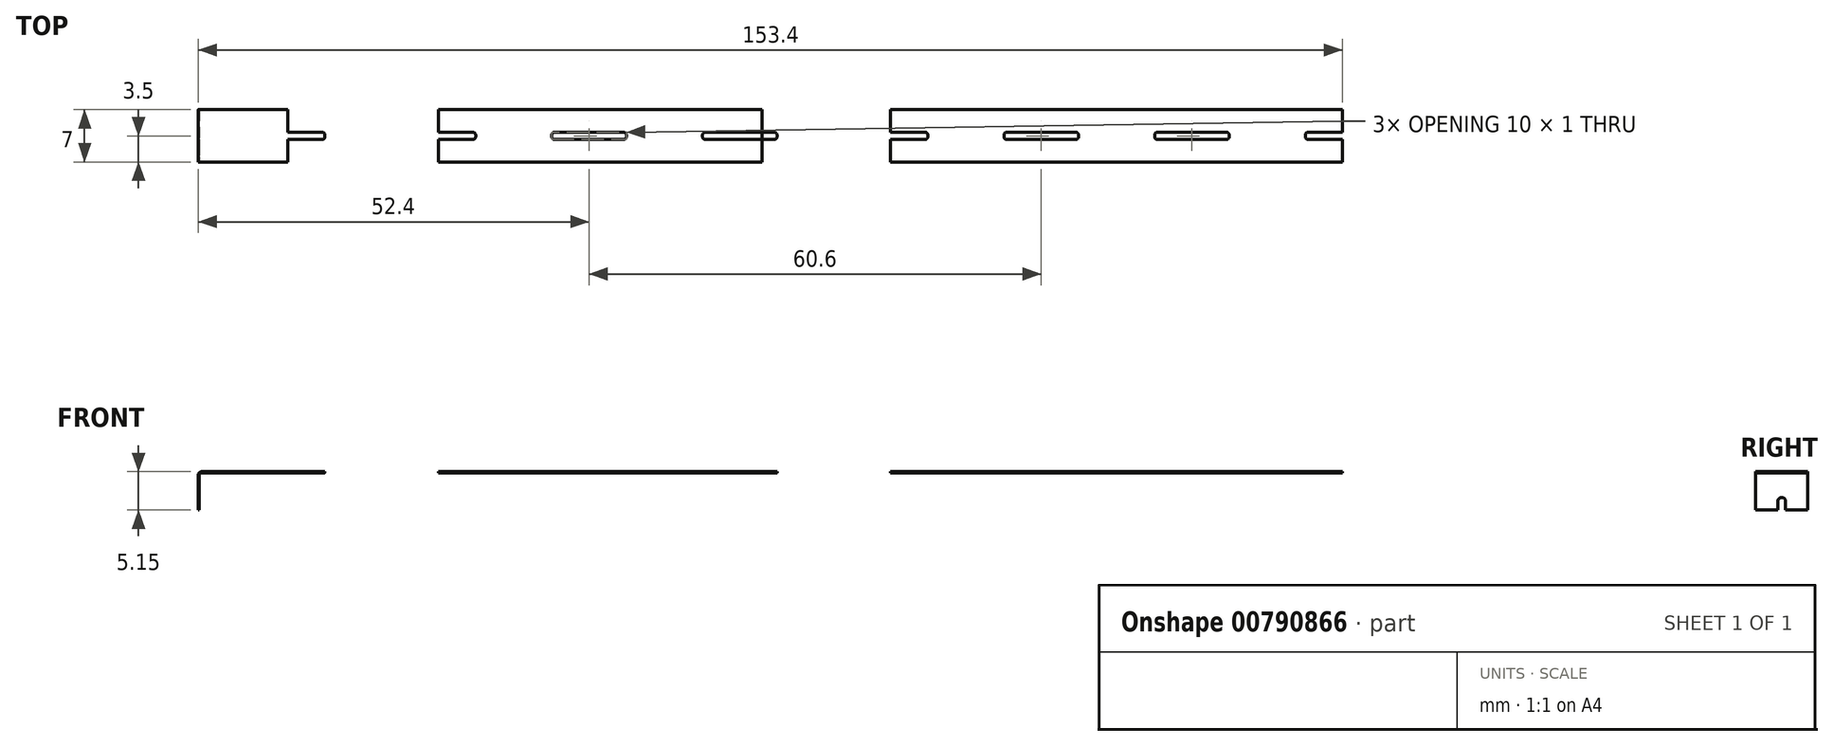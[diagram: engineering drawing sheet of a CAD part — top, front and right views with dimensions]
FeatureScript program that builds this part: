
annotation { "Feature Type Name" : "Feature", "Feature Type Description" : "" }
export const myFeature = defineFeature(function(context is Context, id is Id, definition is map)
    precondition{}
    {
        {
            var Q0;
            Q0=qCreatedBy(makeId("Top.planeOp"),FACE);
            var sketch = newSketch(context, id + "F0", { "sketchPlane" : qUnion([Q0])});
            skPoint(sketch, "E0.middle", {"position": v(0, 0) * mm});
            skLineSegment(sketch, "E1.bottom", {"start": v(-5.5, -0.5) * mm, "end": v(-10.1, -0.5) * mm});
            skLineSegment(sketch, "E1.top", {"start": v(-5.5, 0.5) * mm, "end": v(-10.1, 0.5) * mm});
            skLineSegment(sketch, "E1.left", {"start": v(-5.1, -0.1) * mm, "end": v(-5.1, 0.1) * mm});
            skLineSegment(sketch, "E1.right", {"start": v(-15.1, -0.1) * mm, "end": v(-15.1, 0.1) * mm});
            skPoint(sketch, "E1.middle", {"position": v(-10.1, 0) * mm});
            skPoint(sketch, "E2.visualSharp", {"position": v(-5.1, 0.5) * mm});
            skArc(sketch, "E2.filletArc", {"start": v(-5.1, 0.1) * mm, "mid": v(-5.22, 0.38) * mm, "end": v(-5.5, 0.5) * mm});
            skPoint(sketch, "E3.visualSharp", {"position": v(-5.1, -0.5) * mm});
            skArc(sketch, "E3.filletArc", {"start": v(-5.5, -0.5) * mm, "mid": v(-5.22, -0.38) * mm, "end": v(-5.1, -0.1) * mm});
            skPoint(sketch, "E4.visualSharp", {"position": v(-15.1, 0.5) * mm});
            skArc(sketch, "E4.filletArc", {"start": v(-14.7, 0.5) * mm, "mid": v(-14.98, 0.38) * mm, "end": v(-15.1, 0.1) * mm});
            skPoint(sketch, "E5.visualSharp", {"position": v(-15.1, -0.5) * mm});
            skArc(sketch, "E5.filletArc", {"start": v(-15.1, -0.1) * mm, "mid": v(-14.98, -0.38) * mm, "end": v(-14.7, -0.5) * mm});
            skLineSegment(sketch, "E6", {"start": v(0, 3.5) * mm, "end": v(-10.1, 3.5) * mm});
            skPoint(sketch, "E6.endSnap0", {"position": v(-10.1, 0.5) * mm});
            skLineSegment(sketch, "E7", {"start": v(-10.1, 3.5) * mm, "end": v(-10.1, 0.5) * mm});
            skLineSegment(sketch, "E8.MirrorCS", {"start": v(0, -3.5) * mm, "end": v(-10.1, -3.5) * mm});
            skLineSegment(sketch, "E9.MirrorCS", {"start": v(-10.1, -3.5) * mm, "end": v(-10.1, -0.5) * mm});
            skLineSegment(sketch, "E10.MirrorCS", {"start": v(0, 3.5) * mm, "end": v(10.1, 3.5) * mm});
            skLineSegment(sketch, "E11.MirrorCS", {"start": v(0, -3.5) * mm, "end": v(10.1, -3.5) * mm});
            skLineSegment(sketch, "E12.MirrorCS", {"start": v(5.1, -0.1) * mm, "end": v(5.1, 0.1) * mm});
            skArc(sketch, "E13.MirrorCS", {"start": v(5.1, 0.1) * mm, "mid": v(5.22, 0.38) * mm, "end": v(5.5, 0.5) * mm});
            skArc(sketch, "E14.MirrorCS", {"start": v(15.1, -0.1) * mm, "mid": v(14.98, -0.38) * mm, "end": v(14.7, -0.5) * mm});
            skLineSegment(sketch, "E15.MirrorCS", {"start": v(15.1, -0.1) * mm, "end": v(15.1, 0.1) * mm});
            skArc(sketch, "E16.MirrorCS", {"start": v(14.7, 0.5) * mm, "mid": v(14.98, 0.38) * mm, "end": v(15.1, 0.1) * mm});
            skArc(sketch, "E17.MirrorCS", {"start": v(5.5, -0.5) * mm, "mid": v(5.22, -0.38) * mm, "end": v(5.1, -0.1) * mm});
            skPoint(sketch, "E18.MirrorP", {"position": v(15.1, 0.5) * mm});
            skLineSegment(sketch, "E19.MirrorCS", {"start": v(5.5, 0.5) * mm, "end": v(14.7, 0.5) * mm});
            skLineSegment(sketch, "E20.MirrorCS", {"start": v(5.5, -0.5) * mm, "end": v(14.7, -0.5) * mm});
            skPoint(sketch, "E21.MirrorP", {"position": v(10.1, 0.5) * mm});
            skPoint(sketch, "E22.MirrorP", {"position": v(5.1, 0.5) * mm});
            skPoint(sketch, "E23.MirrorP", {"position": v(15.1, -0.5) * mm});
            skPoint(sketch, "E24.MirrorP", {"position": v(5.1, -0.5) * mm});
            skPoint(sketch, "E25.MirrorP", {"position": v(10.1, 0) * mm});
            skLineSegment(sketch, "E26.MirrorCS", {"start": v(10.1, 3.5) * mm, "end": v(10.1, 0.5) * mm});
            skLineSegment(sketch, "E27.MirrorCS", {"start": v(10.1, -3.5) * mm, "end": v(10.1, -0.5) * mm});
            skPoint(sketch, "E28.1.0.0", {"position": v(25.3, 0.5) * mm});
            skLineSegment(sketch, "E28.1.0.1", {"start": v(20.2, 3.5) * mm, "end": v(30.3, 3.5) * mm});
            skLineSegment(sketch, "E28.1.0.2", {"start": v(25.7, -0.5) * mm, "end": v(34.9, -0.5) * mm});
            skPoint(sketch, "E28.1.0.3", {"position": v(20.2, 0) * mm});
            skLineSegment(sketch, "E28.1.0.4", {"start": v(20.2, -3.5) * mm, "end": v(30.3, -3.5) * mm});
            skPoint(sketch, "E28.1.0.5", {"position": v(30.3, 0.5) * mm});
            skPoint(sketch, "E28.1.0.6", {"position": v(30.3, 0) * mm});
            skPoint(sketch, "E28.1.0.7", {"position": v(35.3, -0.5) * mm});
            skPoint(sketch, "E28.1.0.8", {"position": v(25.3, -0.5) * mm});
            skLineSegment(sketch, "E28.1.0.9", {"start": v(20.2, -3.5) * mm, "end": v(10.1, -3.5) * mm});
            skLineSegment(sketch, "E28.1.0.10", {"start": v(25.7, 0.5) * mm, "end": v(34.9, 0.5) * mm});
            skLineSegment(sketch, "E28.1.0.11", {"start": v(20.2, 3.5) * mm, "end": v(10.1, 3.5) * mm});
            skLineSegment(sketch, "E28.1.0.12", {"start": v(30.3, 3.5) * mm, "end": v(30.3, 0.5) * mm});
            skLineSegment(sketch, "E28.1.0.13", {"start": v(30.3, -3.5) * mm, "end": v(30.3, -0.5) * mm});
            skPoint(sketch, "E28.1.0.14", {"position": v(35.3, 0.5) * mm});
            skArc(sketch, "E28.1.0.15", {"start": v(34.9, 0.5) * mm, "mid": v(35.18, 0.38) * mm, "end": v(35.3, 0.1) * mm});
            skArc(sketch, "E28.1.0.16", {"start": v(25.7, -0.5) * mm, "mid": v(25.42, -0.38) * mm, "end": v(25.3, -0.1) * mm});
            skArc(sketch, "E28.1.0.17", {"start": v(35.3, -0.1) * mm, "mid": v(35.18, -0.38) * mm, "end": v(34.9, -0.5) * mm});
            skArc(sketch, "E28.1.0.18", {"start": v(25.3, 0.1) * mm, "mid": v(25.42, 0.38) * mm, "end": v(25.7, 0.5) * mm});
            skLineSegment(sketch, "E28.1.0.19", {"start": v(25.3, -0.1) * mm, "end": v(25.3, 0.1) * mm});
            skLineSegment(sketch, "E28.1.0.20", {"start": v(35.3, -0.1) * mm, "end": v(35.3, 0.1) * mm});
            skPoint(sketch, "E28.2.0.0", {"position": v(45.5, 0.5) * mm});
            skLineSegment(sketch, "E28.2.0.1", {"start": v(40.4, 3.5) * mm, "end": v(50.5, 3.5) * mm});
            skLineSegment(sketch, "E28.2.0.2", {"start": v(45.9, -0.5) * mm, "end": v(55.1, -0.5) * mm});
            skPoint(sketch, "E28.2.0.3", {"position": v(40.4, 0) * mm});
            skLineSegment(sketch, "E28.2.0.4", {"start": v(40.4, -3.5) * mm, "end": v(50.5, -3.5) * mm});
            skPoint(sketch, "E28.2.0.5", {"position": v(50.5, 0.5) * mm});
            skPoint(sketch, "E28.2.0.6", {"position": v(50.5, 0) * mm});
            skPoint(sketch, "E28.2.0.7", {"position": v(55.5, -0.5) * mm});
            skPoint(sketch, "E28.2.0.8", {"position": v(45.5, -0.5) * mm});
            skLineSegment(sketch, "E28.2.0.9", {"start": v(40.4, -3.5) * mm, "end": v(30.3, -3.5) * mm});
            skLineSegment(sketch, "E28.2.0.10", {"start": v(45.9, 0.5) * mm, "end": v(55.1, 0.5) * mm});
            skLineSegment(sketch, "E28.2.0.11", {"start": v(40.4, 3.5) * mm, "end": v(30.3, 3.5) * mm});
            skLineSegment(sketch, "E28.2.0.12", {"start": v(50.5, 3.5) * mm, "end": v(50.5, 0.5) * mm});
            skLineSegment(sketch, "E28.2.0.13", {"start": v(50.5, -3.5) * mm, "end": v(50.5, -0.5) * mm});
            skPoint(sketch, "E28.2.0.14", {"position": v(55.5, 0.5) * mm});
            skArc(sketch, "E28.2.0.15", {"start": v(55.1, 0.5) * mm, "mid": v(55.38, 0.38) * mm, "end": v(55.5, 0.1) * mm});
            skArc(sketch, "E28.2.0.16", {"start": v(45.9, -0.5) * mm, "mid": v(45.62, -0.38) * mm, "end": v(45.5, -0.1) * mm});
            skArc(sketch, "E28.2.0.17", {"start": v(55.5, -0.1) * mm, "mid": v(55.38, -0.38) * mm, "end": v(55.1, -0.5) * mm});
            skArc(sketch, "E28.2.0.18", {"start": v(45.5, 0.1) * mm, "mid": v(45.62, 0.38) * mm, "end": v(45.9, 0.5) * mm});
            skLineSegment(sketch, "E28.2.0.19", {"start": v(45.5, -0.1) * mm, "end": v(45.5, 0.1) * mm});
            skLineSegment(sketch, "E28.2.0.20", {"start": v(55.5, -0.1) * mm, "end": v(55.5, 0.1) * mm});
            skPoint(sketch, "E28.3.0.0", {"position": v(65.7, 0.5) * mm});
            skLineSegment(sketch, "E28.3.0.1", {"start": v(60.6, 3.5) * mm, "end": v(70.7, 3.5) * mm});
            skLineSegment(sketch, "E28.3.0.2", {"start": v(66.1, -0.5) * mm, "end": v(75.3, -0.5) * mm});
            skPoint(sketch, "E28.3.0.3", {"position": v(60.6, 0) * mm});
            skLineSegment(sketch, "E28.3.0.4", {"start": v(60.6, -3.5) * mm, "end": v(70.7, -3.5) * mm});
            skPoint(sketch, "E28.3.0.5", {"position": v(70.7, 0.5) * mm});
            skPoint(sketch, "E28.3.0.6", {"position": v(70.7, 0) * mm});
            skPoint(sketch, "E28.3.0.7", {"position": v(75.7, -0.5) * mm});
            skPoint(sketch, "E28.3.0.8", {"position": v(65.7, -0.5) * mm});
            skLineSegment(sketch, "E28.3.0.9", {"start": v(60.6, -3.5) * mm, "end": v(50.5, -3.5) * mm});
            skLineSegment(sketch, "E28.3.0.10", {"start": v(66.1, 0.5) * mm, "end": v(75.3, 0.5) * mm});
            skLineSegment(sketch, "E28.3.0.11", {"start": v(60.6, 3.5) * mm, "end": v(50.5, 3.5) * mm});
            skLineSegment(sketch, "E28.3.0.12", {"start": v(70.7, 3.5) * mm, "end": v(70.7, 0.5) * mm});
            skLineSegment(sketch, "E28.3.0.13", {"start": v(70.7, -3.5) * mm, "end": v(70.7, -0.5) * mm});
            skPoint(sketch, "E28.3.0.14", {"position": v(75.7, 0.5) * mm});
            skArc(sketch, "E28.3.0.15", {"start": v(75.3, 0.5) * mm, "mid": v(75.58, 0.38) * mm, "end": v(75.7, 0.1) * mm});
            skArc(sketch, "E28.3.0.16", {"start": v(66.1, -0.5) * mm, "mid": v(65.82, -0.38) * mm, "end": v(65.7, -0.1) * mm});
            skArc(sketch, "E28.3.0.17", {"start": v(75.7, -0.1) * mm, "mid": v(75.58, -0.38) * mm, "end": v(75.3, -0.5) * mm});
            skArc(sketch, "E28.3.0.18", {"start": v(65.7, 0.1) * mm, "mid": v(65.82, 0.38) * mm, "end": v(66.1, 0.5) * mm});
            skLineSegment(sketch, "E28.3.0.19", {"start": v(65.7, -0.1) * mm, "end": v(65.7, 0.1) * mm});
            skLineSegment(sketch, "E28.3.0.20", {"start": v(75.7, -0.1) * mm, "end": v(75.7, 0.1) * mm});
            skLineSegment(sketch, "E28.direction1", {"start": v(-10.1, -3.5) * mm, "end": v(10.1, -3.5) * mm, "construction": true});
            skLineSegment(sketch, "E29", {"start": v(0, 3.5) * mm, "end": v(0, -3.5) * mm});
            skLineSegment(sketch, "E30.bottom", {"start": v(70.7, -3.5) * mm, "end": v(73.7, -3.5) * mm});
            skLineSegment(sketch, "E30.top", {"start": v(70.7, 3.5) * mm, "end": v(73.7, 3.5) * mm});
            skLineSegment(sketch, "E30.left", {"start": v(70.7, -3.5) * mm, "end": v(70.7, 3.5) * mm});
            skLineSegment(sketch, "E30.right", {"start": v(73.7, -3.5) * mm, "end": v(73.7, 3.5) * mm});
            skPoint(sketch, "E31.0.4.0", {"position": v(85.9, 0.5) * mm});
            skLineSegment(sketch, "E31.1.4.0", {"start": v(80.8, 3.5) * mm, "end": v(90.9, 3.5) * mm});
            skLineSegment(sketch, "E31.4.4.0", {"start": v(86.3, -0.5) * mm, "end": v(95.5, -0.5) * mm});
            skPoint(sketch, "E31.7.4.0", {"position": v(80.8, 0) * mm});
            skLineSegment(sketch, "E31.8.4.0", {"start": v(80.8, -3.5) * mm, "end": v(90.9, -3.5) * mm});
            skPoint(sketch, "E31.11.4.0", {"position": v(90.9, 0.5) * mm});
            skPoint(sketch, "E31.12.4.0", {"position": v(90.9, 0) * mm});
            skPoint(sketch, "E31.13.4.0", {"position": v(95.9, -0.5) * mm});
            skPoint(sketch, "E31.14.4.0", {"position": v(85.9, -0.5) * mm});
            skLineSegment(sketch, "E31.15.4.0", {"start": v(80.8, -3.5) * mm, "end": v(70.7, -3.5) * mm});
            skLineSegment(sketch, "E31.18.4.0", {"start": v(86.3, 0.5) * mm, "end": v(95.5, 0.5) * mm});
            skLineSegment(sketch, "E31.21.4.0", {"start": v(80.8, 3.5) * mm, "end": v(70.7, 3.5) * mm});
            skLineSegment(sketch, "E31.24.4.0", {"start": v(90.9, 3.5) * mm, "end": v(90.9, 0.5) * mm});
            skLineSegment(sketch, "E31.27.4.0", {"start": v(90.9, -3.5) * mm, "end": v(90.9, -0.5) * mm});
            skPoint(sketch, "E31.30.4.0", {"position": v(95.9, 0.5) * mm});
            skArc(sketch, "E31.31.4.0", {"start": v(95.5, 0.5) * mm, "mid": v(95.78, 0.38) * mm, "end": v(95.9, 0.1) * mm});
            skArc(sketch, "E31.35.4.0", {"start": v(86.3, -0.5) * mm, "mid": v(86.02, -0.38) * mm, "end": v(85.9, -0.1) * mm});
            skArc(sketch, "E31.39.4.0", {"start": v(95.9, -0.1) * mm, "mid": v(95.78, -0.38) * mm, "end": v(95.5, -0.5) * mm});
            skArc(sketch, "E31.43.4.0", {"start": v(85.9, 0.1) * mm, "mid": v(86.02, 0.38) * mm, "end": v(86.3, 0.5) * mm});
            skLineSegment(sketch, "E31.47.4.0", {"start": v(85.9, -0.1) * mm, "end": v(85.9, 0.1) * mm});
            skLineSegment(sketch, "E31.50.4.0", {"start": v(95.9, -0.1) * mm, "end": v(95.9, 0.1) * mm});
            skPoint(sketch, "E31.0.5.0", {"position": v(106.1, 0.5) * mm});
            skLineSegment(sketch, "E31.1.5.0", {"start": v(101, 3.5) * mm, "end": v(111.1, 3.5) * mm});
            skLineSegment(sketch, "E31.4.5.0", {"start": v(106.5, -0.5) * mm, "end": v(115.7, -0.5) * mm});
            skPoint(sketch, "E31.7.5.0", {"position": v(101, 0) * mm});
            skLineSegment(sketch, "E31.8.5.0", {"start": v(101, -3.5) * mm, "end": v(111.1, -3.5) * mm});
            skPoint(sketch, "E31.11.5.0", {"position": v(111.1, 0.5) * mm});
            skPoint(sketch, "E31.12.5.0", {"position": v(111.1, 0) * mm});
            skPoint(sketch, "E31.13.5.0", {"position": v(116.1, -0.5) * mm});
            skPoint(sketch, "E31.14.5.0", {"position": v(106.1, -0.5) * mm});
            skLineSegment(sketch, "E31.15.5.0", {"start": v(101, -3.5) * mm, "end": v(90.9, -3.5) * mm});
            skLineSegment(sketch, "E31.18.5.0", {"start": v(106.5, 0.5) * mm, "end": v(115.7, 0.5) * mm});
            skLineSegment(sketch, "E31.21.5.0", {"start": v(101, 3.5) * mm, "end": v(90.9, 3.5) * mm});
            skLineSegment(sketch, "E31.24.5.0", {"start": v(111.1, 3.5) * mm, "end": v(111.1, 0.5) * mm});
            skLineSegment(sketch, "E31.27.5.0", {"start": v(111.1, -3.5) * mm, "end": v(111.1, -0.5) * mm});
            skPoint(sketch, "E31.30.5.0", {"position": v(116.1, 0.5) * mm});
            skArc(sketch, "E31.31.5.0", {"start": v(115.7, 0.5) * mm, "mid": v(115.98, 0.38) * mm, "end": v(116.1, 0.1) * mm});
            skArc(sketch, "E31.35.5.0", {"start": v(106.5, -0.5) * mm, "mid": v(106.22, -0.38) * mm, "end": v(106.1, -0.1) * mm});
            skArc(sketch, "E31.39.5.0", {"start": v(116.1, -0.1) * mm, "mid": v(115.98, -0.38) * mm, "end": v(115.7, -0.5) * mm});
            skArc(sketch, "E31.43.5.0", {"start": v(106.1, 0.1) * mm, "mid": v(106.22, 0.38) * mm, "end": v(106.5, 0.5) * mm});
            skLineSegment(sketch, "E31.47.5.0", {"start": v(106.1, -0.1) * mm, "end": v(106.1, 0.1) * mm});
            skLineSegment(sketch, "E31.50.5.0", {"start": v(116.1, -0.1) * mm, "end": v(116.1, 0.1) * mm});
            skPoint(sketch, "E31.0.6.0", {"position": v(126.3, 0.5) * mm});
            skLineSegment(sketch, "E31.1.6.0", {"start": v(121.2, 3.5) * mm, "end": v(131.3, 3.5) * mm});
            skLineSegment(sketch, "E31.4.6.0", {"start": v(126.7, -0.5) * mm, "end": v(135.9, -0.5) * mm});
            skPoint(sketch, "E31.7.6.0", {"position": v(121.2, 0) * mm});
            skLineSegment(sketch, "E31.8.6.0", {"start": v(121.2, -3.5) * mm, "end": v(131.3, -3.5) * mm});
            skPoint(sketch, "E31.11.6.0", {"position": v(131.3, 0.5) * mm});
            skPoint(sketch, "E31.12.6.0", {"position": v(131.3, 0) * mm});
            skPoint(sketch, "E31.13.6.0", {"position": v(136.3, -0.5) * mm});
            skPoint(sketch, "E31.14.6.0", {"position": v(126.3, -0.5) * mm});
            skLineSegment(sketch, "E31.15.6.0", {"start": v(121.2, -3.5) * mm, "end": v(111.1, -3.5) * mm});
            skLineSegment(sketch, "E31.18.6.0", {"start": v(126.7, 0.5) * mm, "end": v(135.9, 0.5) * mm});
            skLineSegment(sketch, "E31.21.6.0", {"start": v(121.2, 3.5) * mm, "end": v(111.1, 3.5) * mm});
            skLineSegment(sketch, "E31.24.6.0", {"start": v(131.3, 3.5) * mm, "end": v(131.3, 0.5) * mm});
            skLineSegment(sketch, "E31.27.6.0", {"start": v(131.3, -3.5) * mm, "end": v(131.3, -0.5) * mm});
            skPoint(sketch, "E31.30.6.0", {"position": v(136.3, 0.5) * mm});
            skArc(sketch, "E31.31.6.0", {"start": v(135.9, 0.5) * mm, "mid": v(136.18, 0.38) * mm, "end": v(136.3, 0.1) * mm});
            skArc(sketch, "E31.35.6.0", {"start": v(126.7, -0.5) * mm, "mid": v(126.42, -0.38) * mm, "end": v(126.3, -0.1) * mm});
            skArc(sketch, "E31.39.6.0", {"start": v(136.3, -0.1) * mm, "mid": v(136.18, -0.38) * mm, "end": v(135.9, -0.5) * mm});
            skArc(sketch, "E31.43.6.0", {"start": v(126.3, 0.1) * mm, "mid": v(126.42, 0.38) * mm, "end": v(126.7, 0.5) * mm});
            skLineSegment(sketch, "E31.47.6.0", {"start": v(126.3, -0.1) * mm, "end": v(126.3, 0.1) * mm});
            skLineSegment(sketch, "E31.50.6.0", {"start": v(136.3, -0.1) * mm, "end": v(136.3, 0.1) * mm});
            skPoint(sketch, "E31.0.7.0", {"position": v(146.5, 0.5) * mm});
            skLineSegment(sketch, "E31.1.7.0", {"start": v(141.4, 3.5) * mm, "end": v(151.5, 3.5) * mm});
            skLineSegment(sketch, "E31.4.7.0", {"start": v(146.9, -0.5) * mm, "end": v(156.1, -0.5) * mm});
            skPoint(sketch, "E31.7.7.0", {"position": v(141.4, 0) * mm});
            skLineSegment(sketch, "E31.8.7.0", {"start": v(141.4, -3.5) * mm, "end": v(151.5, -3.5) * mm});
            skPoint(sketch, "E31.11.7.0", {"position": v(151.5, 0.5) * mm});
            skPoint(sketch, "E31.12.7.0", {"position": v(151.5, 0) * mm});
            skPoint(sketch, "E31.13.7.0", {"position": v(156.5, -0.5) * mm});
            skPoint(sketch, "E31.14.7.0", {"position": v(146.5, -0.5) * mm});
            skLineSegment(sketch, "E31.15.7.0", {"start": v(141.4, -3.5) * mm, "end": v(131.3, -3.5) * mm});
            skLineSegment(sketch, "E31.18.7.0", {"start": v(146.9, 0.5) * mm, "end": v(156.1, 0.5) * mm});
            skLineSegment(sketch, "E31.21.7.0", {"start": v(141.4, 3.5) * mm, "end": v(131.3, 3.5) * mm});
            skLineSegment(sketch, "E31.24.7.0", {"start": v(151.5, 3.5) * mm, "end": v(151.5, 0.5) * mm});
            skLineSegment(sketch, "E31.27.7.0", {"start": v(151.5, -3.5) * mm, "end": v(151.5, -0.5) * mm});
            skPoint(sketch, "E31.30.7.0", {"position": v(156.5, 0.5) * mm});
            skArc(sketch, "E31.31.7.0", {"start": v(156.1, 0.5) * mm, "mid": v(156.38, 0.38) * mm, "end": v(156.5, 0.1) * mm});
            skArc(sketch, "E31.35.7.0", {"start": v(146.9, -0.5) * mm, "mid": v(146.62, -0.38) * mm, "end": v(146.5, -0.1) * mm});
            skArc(sketch, "E31.39.7.0", {"start": v(156.5, -0.1) * mm, "mid": v(156.38, -0.38) * mm, "end": v(156.1, -0.5) * mm});
            skArc(sketch, "E31.43.7.0", {"start": v(146.5, 0.1) * mm, "mid": v(146.62, 0.38) * mm, "end": v(146.9, 0.5) * mm});
            skLineSegment(sketch, "E31.47.7.0", {"start": v(146.5, -0.1) * mm, "end": v(146.5, 0.1) * mm});
            skLineSegment(sketch, "E31.50.7.0", {"start": v(156.5, -0.1) * mm, "end": v(156.5, 0.1) * mm});
            skSolve(sketch);
        }
        {
            var Q0;
            {var subQ8=sQuery(id+"F0.wireOp",EDGE,"E28.3.0.12");Q0=makeQuery(id+"F0.imprint","IMPRINT",FACE,{"disambiguationData":[TD([[makeQuery(id+"F0.imprint","IMPRINT",EDGE,{"derivedFrom":subQ8}),1.0]])]});}
            var Q1;
            {var subQ3=sQuery(id+"F0.wireOp",EDGE,"E14.MirrorCS");Q1=makeQuery(id+"F0.imprint","IMPRINT",FACE,{"disambiguationData":[TD([[makeQuery(id+"F0.imprint","IMPRINT",EDGE,{"derivedFrom":subQ3}),1.0]])]});}
            var Q2;
            {var subQ8=sQuery(id+"F0.wireOp",EDGE,"E28.1.0.12");Q2=makeQuery(id+"F0.imprint","IMPRINT",FACE,{"disambiguationData":[TD([[makeQuery(id+"F0.imprint","IMPRINT",EDGE,{"derivedFrom":subQ8}),1.0]])]});}
            var Q3;
            {var subQ8=sQuery(id+"F0.wireOp",EDGE,"E28.2.0.12");Q3=makeQuery(id+"F0.imprint","IMPRINT",FACE,{"disambiguationData":[TD([[makeQuery(id+"F0.imprint","IMPRINT",EDGE,{"derivedFrom":subQ8}),1.0]])]});}
            var Q4;
            Q4=makeQuery(id+"F0.imprint","IMPRINT",FACE,{"disambiguationData":[TD([[makeQuery(id+"F0.imprint","IMPRINT",EDGE,{"derivedFrom":sQuery(id+"F0.wireOp",EDGE,"E10.MirrorCS")}),-1.0]])]});
            var Q5;
            {var subQ5=sQuery(id+"F0.wireOp",EDGE,"E30.top");Q5=makeQuery(id+"F0.imprint","IMPRINT",FACE,{"disambiguationData":[TD([[makeQuery(id+"F0.imprint","IMPRINT",EDGE,{"derivedFrom":subQ5}),-1.0]])]});}
            var Q6;
            {var subQ5=sQuery(id+"F0.wireOp",EDGE,"E30.bottom");Q6=makeQuery(id+"F0.imprint","IMPRINT",FACE,{"disambiguationData":[TD([[makeQuery(id+"F0.imprint","IMPRINT",EDGE,{"derivedFrom":subQ5}),1.0]])]});}
            var Q7;
            {var subQ0=sQuery(id+"F0.wireOp",EDGE,"E30.left");var subQ1=sQuery(id+"F0.wireOp",EDGE,"E28.3.0.10");var subQ2=makeQuery(id+"F0.imprint","INTERSECT",VERTEX,{"derivedFrom":[subQ1,subQ0]});Q7=makeQuery(id+"F0.imprint","IMPRINT",FACE,{"disambiguationData":[TD([[makeQuery(id+"F0.imprint","IMPRINT",EDGE,{"disambiguationData":[TD([[subQ2,-1.0]])],"derivedFrom":subQ1}),1.0]])]});}
            var Q8;
            {var subQ15=sQuery(id+"F0.wireOp",EDGE,"E28.3.0.15");Q8=makeQuery(id+"F0.imprint","IMPRINT",FACE,{"disambiguationData":[TD([[makeQuery(id+"F0.imprint","IMPRINT",EDGE,{"derivedFrom":subQ15}),1.0]])]});}
            var Q9;
            {var subQ0=sQuery(id+"F0.wireOp",EDGE,"E30.left");var subQ1=sQuery(id+"F0.wireOp",EDGE,"E28.3.0.2");var subQ2=makeQuery(id+"F0.imprint","INTERSECT",VERTEX,{"derivedFrom":[subQ1,subQ0]});Q9=makeQuery(id+"F0.imprint","IMPRINT",FACE,{"disambiguationData":[TD([[makeQuery(id+"F0.imprint","IMPRINT",EDGE,{"disambiguationData":[TD([[subQ2,-1.0]])],"derivedFrom":subQ1}),-1.0]])]});}
            var Q10;
            {var subQ8=sQuery(id+"F0.wireOp",EDGE,"E31.24.4.0");Q10=makeQuery(id+"F0.imprint","IMPRINT",FACE,{"disambiguationData":[TD([[makeQuery(id+"F0.imprint","IMPRINT",EDGE,{"derivedFrom":subQ8}),1.0]])]});}
            var Q11;
            {var subQ8=sQuery(id+"F0.wireOp",EDGE,"E31.24.5.0");Q11=makeQuery(id+"F0.imprint","IMPRINT",FACE,{"disambiguationData":[TD([[makeQuery(id+"F0.imprint","IMPRINT",EDGE,{"derivedFrom":subQ8}),1.0]])]});}
            var Q12;
            {var subQ8=sQuery(id+"F0.wireOp",EDGE,"E31.24.6.0");Q12=makeQuery(id+"F0.imprint","IMPRINT",FACE,{"disambiguationData":[TD([[makeQuery(id+"F0.imprint","IMPRINT",EDGE,{"derivedFrom":subQ8}),1.0]])]});}
            extrude(context, id + "F1", {"entities" : qUnion([Q0, Q1, Q2, Q3, Q4, Q5, Q6, Q7, Q8, Q9, Q10, Q11, Q12]), "depth" : 0.15 * mm, "offsetDistance" : 25 * mm});
        }
        {
            var Q0;
            Q0=makeQuery(id+"F1.opExtrude","SWEPT_FACE",FACE,{"disambiguationData":[OSD([sQuery(id+"F0.wireOp",EDGE,"E29")])]});
            extrude(context, id + "F2", {"entities" : qUnion([Q0]), "operationType" : NewBodyOperationType.ADD, "depth" : 1.9 * mm, "offsetDistance" : 25 * mm});
        }
        {
            var Q0;
            {var subQ0=sQuery(id+"F0.wireOp",EDGE,"E29");Q0=makeQuery(id+"F2.boolean.opBoolean","MERGE",FACE,{"derivedFrom":[makeQuery(id+"F1.opExtrude","CAP_FACE",FACE,{"disambiguationData":[OSD([sQuery(id+"F0.wireOp",EDGE,"E10.MirrorCS"),sQuery(id+"F0.wireOp",EDGE,"E11.MirrorCS"),sQuery(id+"F0.wireOp",EDGE,"E12.MirrorCS"),sQuery(id+"F0.wireOp",EDGE,"E13.MirrorCS"),sQuery(id+"F0.wireOp",EDGE,"E14.MirrorCS"),sQuery(id+"F0.wireOp",EDGE,"E15.MirrorCS"),sQuery(id+"F0.wireOp",EDGE,"E16.MirrorCS"),sQuery(id+"F0.wireOp",EDGE,"E17.MirrorCS"),sQuery(id+"F0.wireOp",EDGE,"E19.MirrorCS"),sQuery(id+"F0.wireOp",EDGE,"E20.MirrorCS"),sQuery(id+"F0.wireOp",EDGE,"E28.1.0.1"),sQuery(id+"F0.wireOp",EDGE,"E28.1.0.2"),sQuery(id+"F0.wireOp",EDGE,"E28.1.0.4"),sQuery(id+"F0.wireOp",EDGE,"E28.1.0.9"),sQuery(id+"F0.wireOp",EDGE,"E28.1.0.10"),sQuery(id+"F0.wireOp",EDGE,"E28.1.0.11"),sQuery(id+"F0.wireOp",EDGE,"E28.1.0.15"),sQuery(id+"F0.wireOp",EDGE,"E28.1.0.16"),sQuery(id+"F0.wireOp",EDGE,"E28.1.0.17"),sQuery(id+"F0.wireOp",EDGE,"E28.1.0.18"),sQuery(id+"F0.wireOp",EDGE,"E28.1.0.19"),sQuery(id+"F0.wireOp",EDGE,"E28.1.0.20"),sQuery(id+"F0.wireOp",EDGE,"E28.2.0.1"),sQuery(id+"F0.wireOp",EDGE,"E28.2.0.2"),sQuery(id+"F0.wireOp",EDGE,"E28.2.0.4"),sQuery(id+"F0.wireOp",EDGE,"E28.2.0.9"),sQuery(id+"F0.wireOp",EDGE,"E28.2.0.10"),sQuery(id+"F0.wireOp",EDGE,"E28.2.0.11"),sQuery(id+"F0.wireOp",EDGE,"E28.2.0.15"),sQuery(id+"F0.wireOp",EDGE,"E28.2.0.16"),sQuery(id+"F0.wireOp",EDGE,"E28.2.0.17"),sQuery(id+"F0.wireOp",EDGE,"E28.2.0.18"),sQuery(id+"F0.wireOp",EDGE,"E28.2.0.19"),sQuery(id+"F0.wireOp",EDGE,"E28.2.0.20"),sQuery(id+"F0.wireOp",EDGE,"E28.3.0.1"),sQuery(id+"F0.wireOp",EDGE,"E28.3.0.2"),sQuery(id+"F0.wireOp",EDGE,"E28.3.0.4"),sQuery(id+"F0.wireOp",EDGE,"E28.3.0.9"),sQuery(id+"F0.wireOp",EDGE,"E28.3.0.10"),sQuery(id+"F0.wireOp",EDGE,"E28.3.0.11"),sQuery(id+"F0.wireOp",EDGE,"E28.3.0.12"),sQuery(id+"F0.wireOp",EDGE,"E28.3.0.13"),sQuery(id+"F0.wireOp",EDGE,"E28.3.0.16"),sQuery(id+"F0.wireOp",EDGE,"E28.3.0.18"),sQuery(id+"F0.wireOp",EDGE,"E28.3.0.19"),subQ0])],"isStart":true}),makeQuery(id+"F2.opExtrude","SWEPT_FACE",FACE,{"disambiguationData":[OSD([subQ0]),TDD([makeQuery(id+"F1.opExtrude","CAP_EDGE",EDGE,{"disambiguationData":[OSD([subQ0])],"isStart":true})])]})]});}
            var sketch = newSketch(context, id + "F3", { "sketchPlane" : qUnion([Q0])});
            skLineSegment(sketch, "E32.bottom", {"start": v(-1.9, -3.5) * mm, "end": v(-1.75, -3.5) * mm});
            skLineSegment(sketch, "E32.top", {"start": v(-1.9, 3.5) * mm, "end": v(-1.75, 3.5) * mm});
            skLineSegment(sketch, "E32.left", {"start": v(-1.9, -3.5) * mm, "end": v(-1.9, 3.5) * mm});
            skLineSegment(sketch, "E32.right", {"start": v(-1.75, -3.5) * mm, "end": v(-1.75, 3.5) * mm});
            skSolve(sketch);
        }
        {
            var Q0;
            Q0=qSketchRegion(id+"F3",true);
            extrude(context, id + "F4", {"entities" : qUnion([Q0]), "operationType" : NewBodyOperationType.ADD, "depth" : 5 * mm, "offsetDistance" : 25 * mm});
        }
        {
            var Q0;
            Q0=makeQuery(id+"F4.boolean.opBoolean","MERGE",FACE,{"derivedFrom":[makeQuery(id+"F2.opExtrude","CAP_FACE",FACE,{"disambiguationData":[OSD([sQuery(id+"F0.wireOp",EDGE,"E29")])],"isStart":false}),makeQuery(id+"F4.opExtrude","SWEPT_FACE",FACE,{"disambiguationData":[OSD([sQuery(id+"F3.wireOp",EDGE,"E32.left")])]})]});
            var sketch = newSketch(context, id + "F5", { "sketchPlane" : qUnion([Q0])});
            skLineSegment(sketch, "E33.bottom", {"start": v(0.1, -3.35) * mm, "end": v(-0.1, -3.35) * mm});
            skLineSegment(sketch, "E33.top", {"start": v(0.5, -13.35) * mm, "end": v(-0.5, -13.35) * mm});
            skLineSegment(sketch, "E33.left", {"start": v(0.5, -3.75) * mm, "end": v(0.5, -13.35) * mm});
            skLineSegment(sketch, "E33.right", {"start": v(-0.5, -3.75) * mm, "end": v(-0.5, -13.35) * mm});
            skPoint(sketch, "E33.middle", {"position": v(0, -8.35) * mm});
            skPoint(sketch, "E33.middle.positionSnap0", {"position": v(0, -5) * mm});
            skPoint(sketch, "E33.centerSnap0", {"position": v(0, -5) * mm});
            skPoint(sketch, "E34.visualSharp", {"position": v(-0.5, -3.35) * mm});
            skArc(sketch, "E34.filletArc", {"start": v(-0.1, -3.35) * mm, "mid": v(-0.38, -3.47) * mm, "end": v(-0.5, -3.75) * mm});
            skPoint(sketch, "E35.visualSharp", {"position": v(0.5, -3.35) * mm});
            skArc(sketch, "E35.filletArc", {"start": v(0.5, -3.75) * mm, "mid": v(0.38, -3.47) * mm, "end": v(0.1, -3.35) * mm});
            skSolve(sketch);
        }
        {
            var Q0;
            Q0=makeQuery(id+"F5.imprint","IMPRINT",FACE,{"disambiguationData":[TD([[makeQuery(id+"F5.imprint","IMPRINT",EDGE,{"derivedFrom":sQuery(id+"F5.wireOp",EDGE,"E33.bottom")}),1.0]])]});
            extrude(context, id + "F6", {"entities" : qUnion([Q0]), "operationType" : NewBodyOperationType.REMOVE, "oppositeDirection" : true, "depth" : 25 * mm, "offsetDistance" : 25 * mm});
        }
        {
            var Q0;
            {var subQ0=sQuery(id+"F0.wireOp",EDGE,"E29");Q0=makeQuery(id+"F2.opExtrude","CAP_EDGE",EDGE,{"disambiguationData":[OSD([subQ0]),TDD([makeQuery(id+"F1.opExtrude","CAP_EDGE",EDGE,{"disambiguationData":[OSD([subQ0])],"isStart":false})])],"isStart":false});}
            var Q1;
            Q1=makeQuery(id+"F4.opExtrude","CAP_EDGE",EDGE,{"disambiguationData":[OSD([sQuery(id+"F3.wireOp",EDGE,"E32.right")])],"isStart":true});
            fillet(context, id + "F7", {"entities" : qUnion([Q0, Q1]), "radius" : 0.5 * mm, "tangentPropagation" : true, "allowEdgeOverflow" : false});
        }
    });
